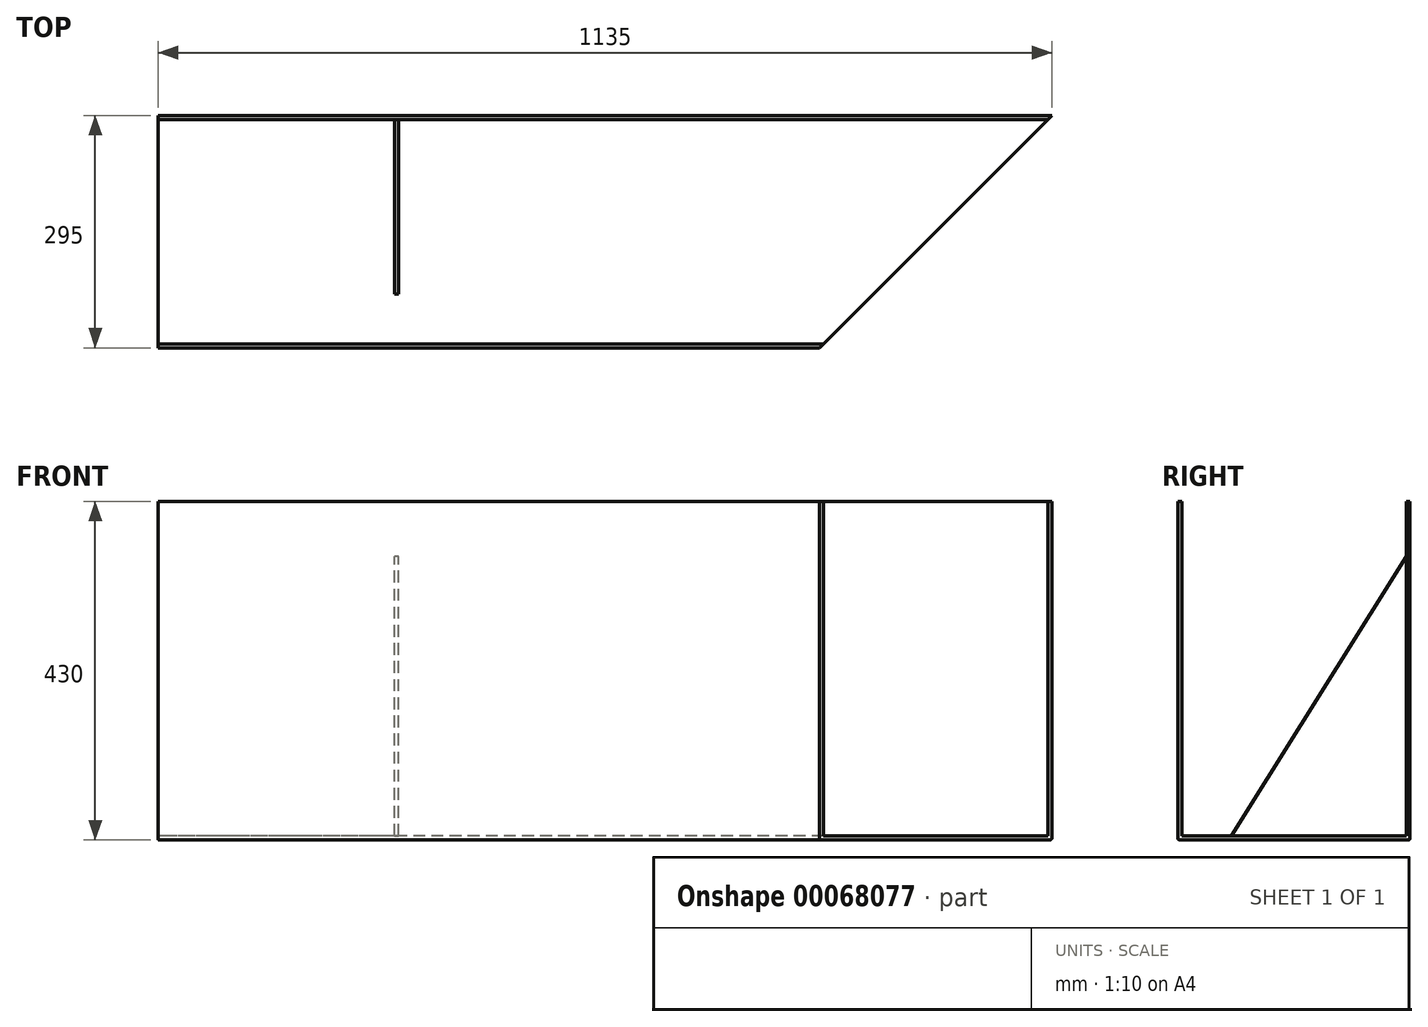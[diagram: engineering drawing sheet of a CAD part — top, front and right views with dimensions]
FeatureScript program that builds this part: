
annotation { "Feature Type Name" : "Feature", "Feature Type Description" : "" }
export const myFeature = defineFeature(function(context is Context, id is Id, definition is map)
    precondition{}
    {
        {
            var Q0;
            Q0=qCreatedBy(makeId("Right.planeOp"),FACE);
            var sketch = newSketch(context, id + "F0", { "sketchPlane" : qUnion([Q0])});
            skLineSegment(sketch, "E0.left", {"start": v(0, 0) * mm, "end": v(0, 430) * mm});
            skLineSegment(sketch, "E1", {"start": v(0, 0) * mm, "end": v(-295, 0) * mm});
            skLineSegment(sketch, "E2", {"start": v(-295, 0) * mm, "end": v(-295, 430) * mm});
            skLineSegment(sketch, "E3.0", {"start": v(-290, 5) * mm, "end": v(-290, 430) * mm});
            skLineSegment(sketch, "E3.1", {"start": v(-5, 5) * mm, "end": v(-290, 5) * mm});
            skLineSegment(sketch, "E3.2", {"start": v(-5, 5) * mm, "end": v(-5, 430) * mm});
            skLineSegment(sketch, "E4", {"start": v(0, 430) * mm, "end": v(-5, 430) * mm});
            skLineSegment(sketch, "E5", {"start": v(-290, 430) * mm, "end": v(-295, 430) * mm});
            skSolve(sketch);
        }
        {
            var Q0;
            Q0=makeQuery(id+"F0.imprint","IMPRINT",FACE,{"disambiguationData":[TD([[makeQuery(id+"F0.imprint","IMPRINT",EDGE,{"derivedFrom":sQuery(id+"F0.wireOp",EDGE,"E0.bottom")}),-1.0]])]});
            var Q1;
            Q1=makeQuery(id+"F0.imprint","IMPRINT",FACE,{"disambiguationData":[TD([[makeQuery(id+"F0.imprint","IMPRINT",EDGE,{"derivedFrom":sQuery(id+"F0.wireOp",EDGE,"E0.left")}),1.0]])]});
            extrude(context, id + "F1", {"entities" : qUnion([Q0, Q1]), "depth" : 1200 * mm});
        }
        {
            var Q0;
            Q0=qCreatedBy(makeId("Right.planeOp"),FACE);
            cPlane(context, id + "F2", {"entities" : qUnion([Q0]), "cplaneType" : CPlaneType.OFFSET, "offset" : 300 * mm, "width" : 150 * mm, "height" : 150 * mm});
        }
        {
            var Q0;
            Q0=qCreatedBy(id+"F2.planeOp",FACE);
            var sketch = newSketch(context, id + "F3", { "sketchPlane" : qUnion([Q0])});
            skLineSegment(sketch, "E6.0", {"start": v(-5, 0) * mm, "end": v(-5, 360) * mm});
            skLineSegment(sketch, "E7.0", {"start": v(-5, 0) * mm, "end": v(-230, 0) * mm});
            skPoint(sketch, "E8", {"position": v(-230, 0) * mm});
            skPoint(sketch, "E9", {"position": v(-5, 360) * mm});
            skLineSegment(sketch, "E10", {"start": v(-5, 360) * mm, "end": v(-230, 0) * mm});
            skSolve(sketch);
        }
        {
            var Q0;
            Q0=makeQuery(id+"F3.imprint","IMPRINT",FACE,{"disambiguationData":[TD([[makeQuery(id+"F3.imprint","IMPRINT",EDGE,{"derivedFrom":sQuery(id+"F3.wireOp",EDGE,"E6.0")}),1.0]])]});
            extrude(context, id + "F4", {"entities" : qUnion([Q0]), "depth" : 5 * mm});
        }
        {
            var Q0;
            Q0=qCreatedBy(makeId("Top.planeOp"),FACE);
            var sketch = newSketch(context, id + "F5", { "sketchPlane" : qUnion([Q0])});
            skLineSegment(sketch, "E11.bottom", {"start": v(0, 0) * mm, "end": v(1200, 0) * mm});
            skLineSegment(sketch, "E11.top", {"start": v(0, -230) * mm, "end": v(1200, -230) * mm});
            skLineSegment(sketch, "E11.left", {"start": v(0, 0) * mm, "end": v(0, -230) * mm});
            skLineSegment(sketch, "E11.right", {"start": v(1200, 0) * mm, "end": v(1200, -230) * mm});
            skSolve(sketch);
        }
        {
            var Q0;
            Q0=makeQuery(id+"F5.imprint","IMPRINT",FACE,{"disambiguationData":[TD([[makeQuery(id+"F5.imprint","IMPRINT",EDGE,{"derivedFrom":sQuery(id+"F5.wireOp",EDGE,"E11.bottom")}),-1.0]])]});
            extrude(context, id + "F6", {"entities" : qUnion([Q0]), "operationType" : NewBodyOperationType.ADD, "depth" : 4 * mm});
        }
        {
            var Q0;
            Q0=makeQuery(id+"F1.opExtrude","SWEPT_EDGE",EDGE,{"disambiguationData":[OSD([sQuery(id+"F0.wireOp",EDGE,"E0.left"),sQuery(id+"F0.wireOp",EDGE,"E1")])]});
            var Q1;
            Q1=makeQuery(id+"F1.opExtrude","SWEPT_EDGE",EDGE,{"disambiguationData":[OSD([sQuery(id+"F0.wireOp",EDGE,"E1"),sQuery(id+"F0.wireOp",EDGE,"E2")])]});
            fillet(context, id + "F7", {"entities" : qUnion([Q0, Q1]), "radius" : 2 * mm, "tangentPropagation" : true, "allowEdgeOverflow" : false});
        }
        {
            var Q0;
            Q0=makeQuery(id+"F1.opExtrude","SWEPT_FACE",FACE,{"disambiguationData":[OSD([sQuery(id+"F0.wireOp",EDGE,"E4")])]});
            var sketch = newSketch(context, id + "F8", { "sketchPlane" : qUnion([Q0])});
            skLineSegment(sketch, "E12.top", {"start": v(0, -295) * mm, "end": v(840, -295) * mm, "construction": true});
            skLineSegment(sketch, "E13", {"start": v(840, -295) * mm, "end": v(1135, 0) * mm});
            skLineSegment(sketch, "E14", {"start": v(840, -295) * mm, "end": v(1200, -295) * mm});
            skLineSegment(sketch, "E15", {"start": v(1200, -295) * mm, "end": v(1200, 0) * mm});
            skLineSegment(sketch, "E16", {"start": v(1200, 0) * mm, "end": v(1135, 0) * mm});
            skSolve(sketch);
        }
        {
            var Q0;
            Q0 = qSketchRegion(id + "F8", true);
            extrude(context, id + "F9", {"entities" : qUnion([Q0]), "operationType" : NewBodyOperationType.REMOVE, "endBound" : BoundingType.THROUGH_ALL, "oppositeDirection" : true, "depth" : 25 * mm});
        }
    });
